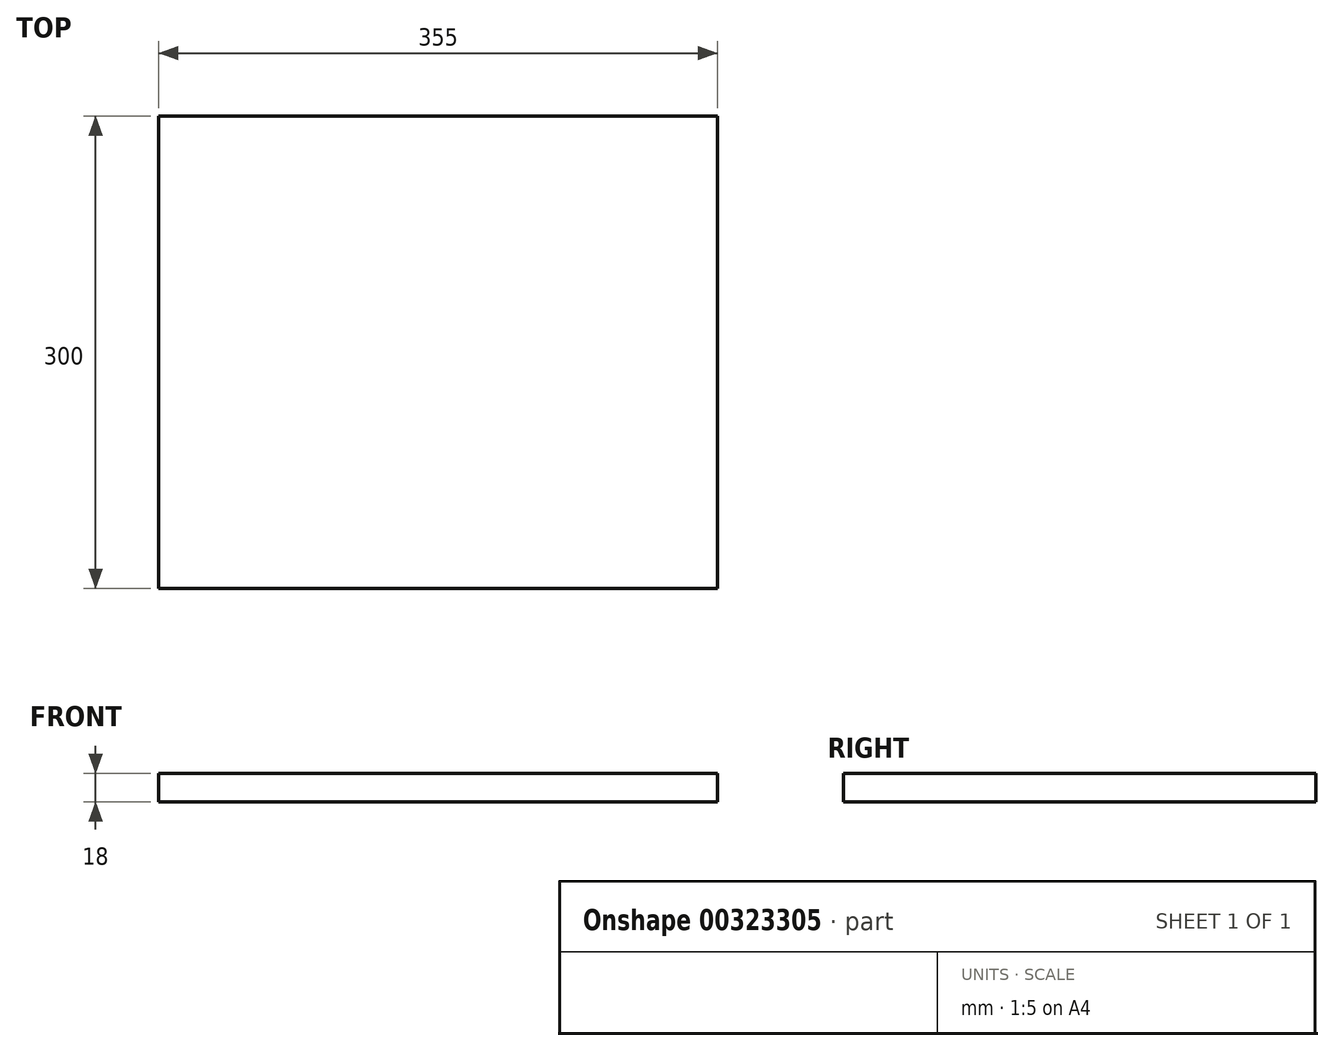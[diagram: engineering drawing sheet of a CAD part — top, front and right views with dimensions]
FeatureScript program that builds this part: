
annotation { "Feature Type Name" : "Feature", "Feature Type Description" : "" }
export const myFeature = defineFeature(function(context is Context, id is Id, definition is map)
    precondition{}
    {
        {
            var Q0;
            Q0=qCreatedBy(makeId("Top.planeOp"),FACE);
            var sketch = newSketch(context, id + "F0", { "sketchPlane" : qUnion([Q0])});
            skLineSegment(sketch, "E0.bottom", {"start": v(0, 0) * mm, "end": v(355, 0) * mm});
            skLineSegment(sketch, "E0.top", {"start": v(0, 300) * mm, "end": v(355, 300) * mm});
            skLineSegment(sketch, "E0.left", {"start": v(0, 0) * mm, "end": v(0, 300) * mm});
            skLineSegment(sketch, "E0.right", {"start": v(355, 0) * mm, "end": v(355, 300) * mm});
            skSolve(sketch);
        }
        {
            var Q0;
            Q0 = qSketchRegion(id + "F0", true);
            extrude(context, id + "F1", {"entities" : qUnion([Q0]), "depth" : 18 * mm, "offsetDistance" : 25 * mm});
        }
    });
